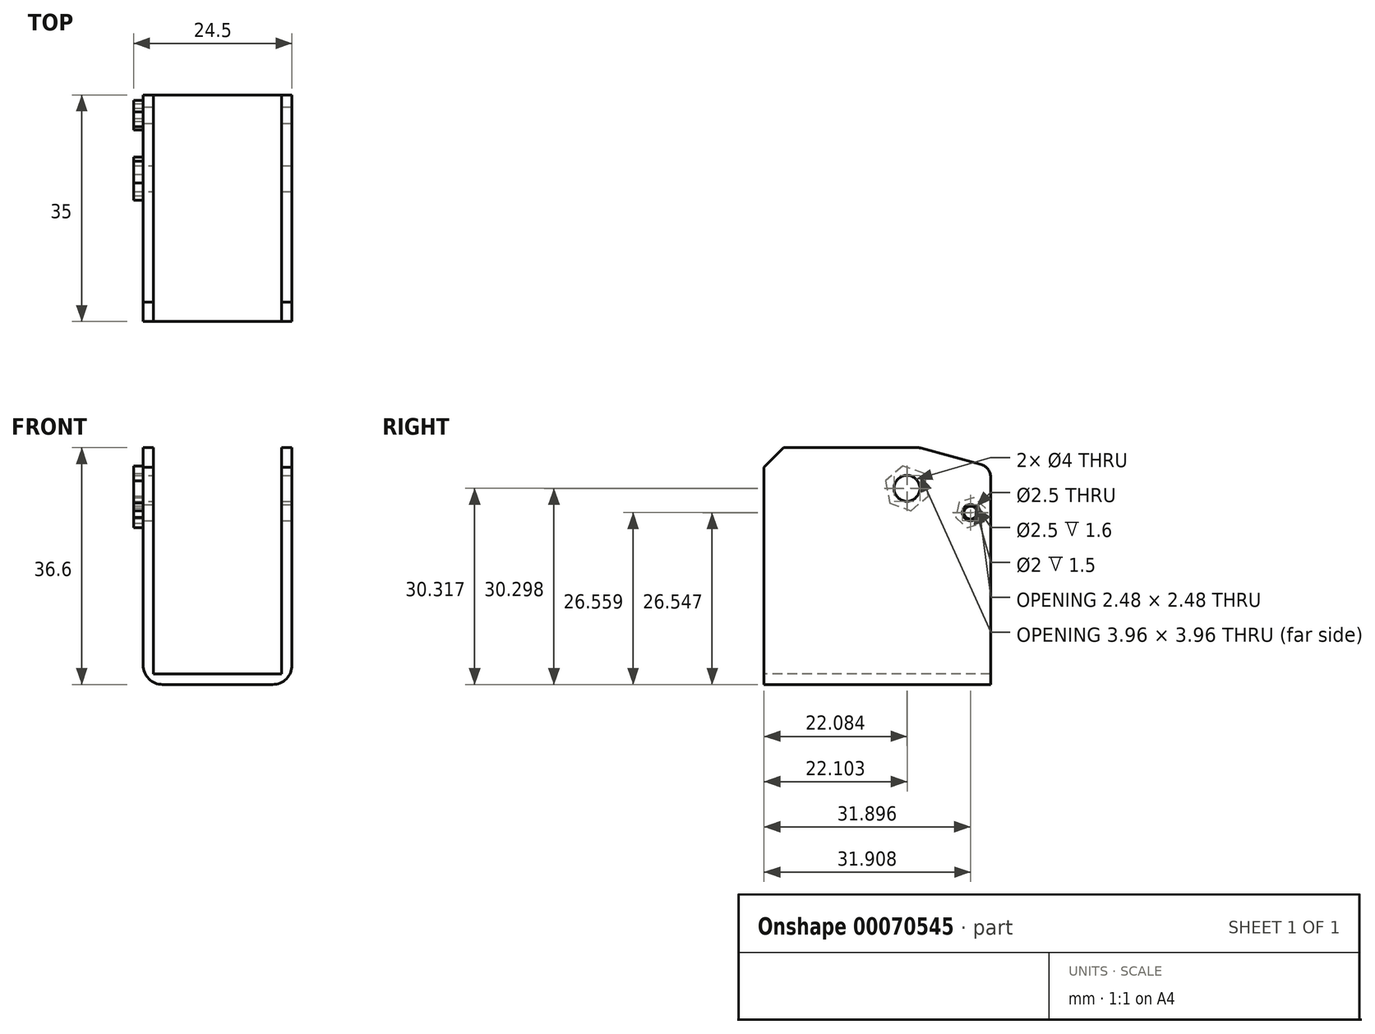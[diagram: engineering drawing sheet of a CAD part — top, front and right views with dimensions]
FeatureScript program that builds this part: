
annotation { "Feature Type Name" : "Feature", "Feature Type Description" : "" }
export const myFeature = defineFeature(function(context is Context, id is Id, definition is map)
    precondition{}
    {
        {
            var Q0;
            Q0=qCreatedBy(makeId("Top.planeOp"),FACE);
            var sketch = newSketch(context, id + "F0", { "sketchPlane" : qUnion([Q0])});
            skLineSegment(sketch, "E0.bottom", {"start": v(-7.08, 17.17) * mm, "end": v(15.92, 17.17) * mm});
            skLineSegment(sketch, "E0.top", {"start": v(-7.08, -17.83) * mm, "end": v(15.92, -17.83) * mm});
            skLineSegment(sketch, "E0.left", {"start": v(-7.08, 17.17) * mm, "end": v(-7.08, -17.83) * mm});
            skLineSegment(sketch, "E0.right", {"start": v(15.92, 17.17) * mm, "end": v(15.92, -17.83) * mm});
            skSolve(sketch);
        }
        {
            var Q0;
            Q0 = qSketchRegion(id + "F0", true);
            extrude(context, id + "F1", {"entities" : qUnion([Q0]), "depth" : 1.6 * mm});
        }
        {
            var Q0;
            Q0=makeQuery(id+"F1.opExtrude","CAP_FACE",FACE,{"disambiguationData":[OSD([sQuery(id+"F0.wireOp",EDGE,"E0.bottom"),sQuery(id+"F0.wireOp",EDGE,"E0.top"),sQuery(id+"F0.wireOp",EDGE,"E0.left"),sQuery(id+"F0.wireOp",EDGE,"E0.right")])],"isStart":false});
            var sketch = newSketch(context, id + "F2", { "sketchPlane" : qUnion([Q0])});
            skLineSegment(sketch, "E1.bottom", {"start": v(-7.08, 17.17) * mm, "end": v(-5.48, 17.17) * mm});
            skLineSegment(sketch, "E1.top", {"start": v(-7.08, -17.83) * mm, "end": v(-5.48, -17.83) * mm});
            skLineSegment(sketch, "E1.left", {"start": v(-7.08, 17.17) * mm, "end": v(-7.08, -17.83) * mm});
            skLineSegment(sketch, "E1.right", {"start": v(-5.48, 17.17) * mm, "end": v(-5.48, -17.83) * mm});
            skLineSegment(sketch, "E2.bottom", {"start": v(15.92, 17.17) * mm, "end": v(14.32, 17.17) * mm});
            skLineSegment(sketch, "E2.top", {"start": v(15.92, -17.83) * mm, "end": v(14.32, -17.83) * mm});
            skLineSegment(sketch, "E2.left", {"start": v(15.92, 17.17) * mm, "end": v(15.92, -17.83) * mm});
            skLineSegment(sketch, "E2.right", {"start": v(14.32, 17.17) * mm, "end": v(14.32, -17.83) * mm});
            skSolve(sketch);
        }
        {
            var Q0;
            Q0 = qSketchRegion(id + "F2", true);
            extrude(context, id + "F3", {"entities" : qUnion([Q0]), "operationType" : NewBodyOperationType.ADD, "depth" : 35 * mm});
        }
        {
            var Q0;
            Q0=makeQuery(id+"F3.opExtrude","CAP_EDGE",EDGE,{"disambiguationData":[OSD([sQuery(id+"F2.wireOp",EDGE,"E2.right")])],"isStart":true});
            var Q1;
            Q1=makeQuery(id+"F1.opExtrude","CAP_EDGE",EDGE,{"disambiguationData":[OSD([sQuery(id+"F0.wireOp",EDGE,"E0.right")])],"isStart":true});
            var Q2;
            Q2=makeQuery(id+"F1.opExtrude","CAP_EDGE",EDGE,{"disambiguationData":[OSD([sQuery(id+"F0.wireOp",EDGE,"E0.left")])],"isStart":true});
            var Q3;
            Q3=makeQuery(id+"F3.opExtrude","CAP_EDGE",EDGE,{"disambiguationData":[OSD([sQuery(id+"F2.wireOp",EDGE,"E1.right")])],"isStart":true});
            fillet(context, id + "F4", {"entities" : qUnion([Q0, Q1, Q2, Q3]), "radius" : 3 * mm, "tangentPropagation" : true, "allowEdgeOverflow" : false});
        }
        {
            var Q0;
            Q0=makeQuery(id+"F3.opExtrude","CAP_EDGE",EDGE,{"disambiguationData":[OSD([sQuery(id+"F2.wireOp",EDGE,"E2.bottom")])],"isStart":false});
            var Q1;
            Q1=makeQuery(id+"F3.opExtrude","CAP_EDGE",EDGE,{"disambiguationData":[OSD([sQuery(id+"F2.wireOp",EDGE,"E1.bottom")])],"isStart":false});
            chamfer(context, id + "F5", {"entities" : qUnion([Q0, Q1]), "chamferType" : ChamferType.TWO_OFFSETS, "width1" : 3 * mm, "oppositeDirection" : false, "width2" : 11 * mm, "tangentPropagation" : true});
        }
        {
            var Q0;
            {var subQ0=sQuery(id+"F2.wireOp",EDGE,"E2.bottom");Q0=makeQuery(id+"F5.opChamfer","BLEND_EDGE",EDGE,{"blendedFrom":[makeQuery(id+"F3.opExtrude","CAP_EDGE",EDGE,{"disambiguationData":[OSD([subQ0])],"isStart":false}),makeQuery(id+"F3.boolean.opBoolean","MERGE",FACE,{"derivedFrom":[makeQuery(id+"F1.opExtrude","SWEPT_FACE",FACE,{"disambiguationData":[OSD([sQuery(id+"F0.wireOp",EDGE,"E0.bottom")])]}),makeQuery(id+"F3.opExtrude","SWEPT_FACE",FACE,{"disambiguationData":[OSD([sQuery(id+"F2.wireOp",EDGE,"E1.bottom")])]}),makeQuery(id+"F3.opExtrude","SWEPT_FACE",FACE,{"disambiguationData":[OSD([subQ0])]})]})],"blendedInto":[makeQuery(id+"F3.boolean.opBoolean","MERGE",FACE,{"derivedFrom":[makeQuery(id+"F1.opExtrude","SWEPT_FACE",FACE,{"disambiguationData":[OSD([sQuery(id+"F0.wireOp",EDGE,"E0.bottom")])]}),makeQuery(id+"F3.opExtrude","SWEPT_FACE",FACE,{"disambiguationData":[OSD([sQuery(id+"F2.wireOp",EDGE,"E1.bottom")])]}),makeQuery(id+"F3.opExtrude","SWEPT_FACE",FACE,{"disambiguationData":[OSD([subQ0])]})]})]});}
            var Q1;
            {var subQ0=sQuery(id+"F2.wireOp",EDGE,"E1.bottom");Q1=makeQuery(id+"F5.opChamfer","BLEND_EDGE",EDGE,{"blendedFrom":[makeQuery(id+"F3.opExtrude","CAP_EDGE",EDGE,{"disambiguationData":[OSD([subQ0])],"isStart":false}),makeQuery(id+"F3.boolean.opBoolean","MERGE",FACE,{"derivedFrom":[makeQuery(id+"F1.opExtrude","SWEPT_FACE",FACE,{"disambiguationData":[OSD([sQuery(id+"F0.wireOp",EDGE,"E0.bottom")])]}),makeQuery(id+"F3.opExtrude","SWEPT_FACE",FACE,{"disambiguationData":[OSD([subQ0])]}),makeQuery(id+"F3.opExtrude","SWEPT_FACE",FACE,{"disambiguationData":[OSD([sQuery(id+"F2.wireOp",EDGE,"E2.bottom")])]})]})],"blendedInto":[makeQuery(id+"F3.boolean.opBoolean","MERGE",FACE,{"derivedFrom":[makeQuery(id+"F1.opExtrude","SWEPT_FACE",FACE,{"disambiguationData":[OSD([sQuery(id+"F0.wireOp",EDGE,"E0.bottom")])]}),makeQuery(id+"F3.opExtrude","SWEPT_FACE",FACE,{"disambiguationData":[OSD([subQ0])]}),makeQuery(id+"F3.opExtrude","SWEPT_FACE",FACE,{"disambiguationData":[OSD([sQuery(id+"F2.wireOp",EDGE,"E2.bottom")])]})]})]});}
            fillet(context, id + "F6", {"entities" : qUnion([Q0, Q1]), "radius" : 2 * mm, "tangentPropagation" : true, "allowEdgeOverflow" : false});
        }
        {
            var Q0;
            {var subQ0=sQuery(id+"F2.wireOp",EDGE,"E2.bottom");Q0=makeQuery(id+"F5.opChamfer","BLEND_EDGE",EDGE,{"blendedFrom":[makeQuery(id+"F3.opExtrude","CAP_EDGE",EDGE,{"disambiguationData":[OSD([subQ0])],"isStart":false}),makeQuery(id+"F3.opExtrude","CAP_FACE",FACE,{"disambiguationData":[OSD([subQ0,sQuery(id+"F2.wireOp",EDGE,"E2.top"),sQuery(id+"F2.wireOp",EDGE,"E2.left"),sQuery(id+"F2.wireOp",EDGE,"E2.right")])],"isStart":false})],"blendedInto":[makeQuery(id+"F3.opExtrude","CAP_FACE",FACE,{"disambiguationData":[OSD([subQ0,sQuery(id+"F2.wireOp",EDGE,"E2.top"),sQuery(id+"F2.wireOp",EDGE,"E2.left"),sQuery(id+"F2.wireOp",EDGE,"E2.right")])],"isStart":false})]});}
            var Q1;
            {var subQ0=sQuery(id+"F2.wireOp",EDGE,"E1.bottom");Q1=makeQuery(id+"F5.opChamfer","BLEND_EDGE",EDGE,{"blendedFrom":[makeQuery(id+"F3.opExtrude","CAP_EDGE",EDGE,{"disambiguationData":[OSD([subQ0])],"isStart":false}),makeQuery(id+"F3.opExtrude","CAP_FACE",FACE,{"disambiguationData":[OSD([subQ0,sQuery(id+"F2.wireOp",EDGE,"E1.top"),sQuery(id+"F2.wireOp",EDGE,"E1.left"),sQuery(id+"F2.wireOp",EDGE,"E1.right")])],"isStart":false})],"blendedInto":[makeQuery(id+"F3.opExtrude","CAP_FACE",FACE,{"disambiguationData":[OSD([subQ0,sQuery(id+"F2.wireOp",EDGE,"E1.top"),sQuery(id+"F2.wireOp",EDGE,"E1.left"),sQuery(id+"F2.wireOp",EDGE,"E1.right")])],"isStart":false})]});}
            fillet(context, id + "F7", {"entities" : qUnion([Q0, Q1]), "radius" : 2 * mm, "tangentPropagation" : true, "allowEdgeOverflow" : false});
        }
        {
            var Q0;
            Q0=makeQuery(id+"F3.opExtrude","CAP_EDGE",EDGE,{"disambiguationData":[OSD([sQuery(id+"F2.wireOp",EDGE,"E1.top")])],"isStart":false});
            var Q1;
            Q1=makeQuery(id+"F3.opExtrude","CAP_EDGE",EDGE,{"disambiguationData":[OSD([sQuery(id+"F2.wireOp",EDGE,"E2.top")])],"isStart":false});
            chamfer(context, id + "F8", {"entities" : qUnion([Q0, Q1]), "width" : 3 * mm, "tangentPropagation" : true});
        }
        {
            var Q0;
            Q0=makeQuery(id+"F3.boolean.opBoolean","MERGE",FACE,{"derivedFrom":[makeQuery(id+"F1.opExtrude","SWEPT_FACE",FACE,{"disambiguationData":[OSD([sQuery(id+"F0.wireOp",EDGE,"E0.right")])]}),makeQuery(id+"F3.opExtrude","SWEPT_FACE",FACE,{"disambiguationData":[OSD([sQuery(id+"F2.wireOp",EDGE,"E2.left")])]})]});
            var sketch = newSketch(context, id + "F9", { "sketchPlane" : qUnion([Q0])});
            skLineSegment(sketch, "E3", {"start": v(4.25, 36.4) * mm, "end": v(4.25, 24.23) * mm, "construction": true});
            skLineSegment(sketch, "E4", {"start": v(14.07, 25.7) * mm, "end": v(14.07, 20.92) * mm, "construction": true});
            skCircle(sketch, "E5", {"center": v(4.25, 30.32) * mm, "radius": 2 * mm});
            skCircle(sketch, "E6", {"center": v(14.07, 26.56) * mm, "radius": 1.25 * mm});
            skSolve(sketch);
        }
        {
            var Q0;
            Q0 = qSketchRegion(id + "F9", true);
            extrude(context, id + "F10", {"entities" : qUnion([Q0]), "operationType" : NewBodyOperationType.REMOVE, "oppositeDirection" : true, "depth" : 30 * mm});
        }
        {
            var Q0;
            Q0=makeQuery(id+"F3.boolean.opBoolean","MERGE",FACE,{"derivedFrom":[makeQuery(id+"F1.opExtrude","SWEPT_FACE",FACE,{"disambiguationData":[OSD([sQuery(id+"F0.wireOp",EDGE,"E0.left")])]}),makeQuery(id+"F3.opExtrude","SWEPT_FACE",FACE,{"disambiguationData":[OSD([sQuery(id+"F2.wireOp",EDGE,"E1.left")])]})]});
            var sketch = newSketch(context, id + "F11", { "sketchPlane" : qUnion([Q0])});
            skCircle(sketch, "E7.cCircle", {"center": v(-4.25, 30.32) * mm, "radius": 3.04 * mm, "construction": true});
            skLineSegment(sketch, "E7.0", {"start": v(-7.57, 29.15) * mm, "end": v(-6.92, 32.6) * mm});
            skLineSegment(sketch, "E7.1", {"start": v(-6.92, 32.6) * mm, "end": v(-3.61, 33.77) * mm});
            skLineSegment(sketch, "E7.2", {"start": v(-3.61, 33.77) * mm, "end": v(-0.94, 31.49) * mm});
            skLineSegment(sketch, "E7.3", {"start": v(-0.94, 31.49) * mm, "end": v(-1.58, 28.03) * mm});
            skLineSegment(sketch, "E7.4", {"start": v(-1.58, 28.03) * mm, "end": v(-4.9, 26.86) * mm});
            skLineSegment(sketch, "E7.5", {"start": v(-4.9, 26.86) * mm, "end": v(-7.57, 29.15) * mm});
            skPoint(sketch, "E7.0.midPoint", {"position": v(-7.25, 30.87) * mm});
            skCircle(sketch, "E8.cCircle", {"center": v(-14.07, 26.56) * mm, "radius": 2.07 * mm, "construction": true});
            skLineSegment(sketch, "E8.0", {"start": v(-16.34, 27.29) * mm, "end": v(-14.57, 28.9) * mm});
            skLineSegment(sketch, "E8.1", {"start": v(-14.57, 28.9) * mm, "end": v(-12.3, 28.17) * mm});
            skLineSegment(sketch, "E8.2", {"start": v(-12.3, 28.17) * mm, "end": v(-11.8, 25.83) * mm});
            skLineSegment(sketch, "E8.3", {"start": v(-11.8, 25.83) * mm, "end": v(-13.56, 24.22) * mm});
            skLineSegment(sketch, "E8.4", {"start": v(-13.56, 24.22) * mm, "end": v(-15.83, 24.95) * mm});
            skLineSegment(sketch, "E8.5", {"start": v(-15.83, 24.95) * mm, "end": v(-16.34, 27.29) * mm});
            skPoint(sketch, "E8.0.midPoint", {"position": v(-15.46, 28.1) * mm});
            skSolve(sketch);
        }
        {
            var Q0;
            Q0 = qSketchRegion(id + "F11", true);
            extrude(context, id + "F12", {"entities" : qUnion([Q0]), "operationType" : NewBodyOperationType.ADD, "depth" : 1.5 * mm});
        }
        {
            var Q0;
            Q0=makeQuery(id+"F3.boolean.opBoolean","MERGE",FACE,{"derivedFrom":[makeQuery(id+"F1.opExtrude","SWEPT_FACE",FACE,{"disambiguationData":[OSD([sQuery(id+"F0.wireOp",EDGE,"E0.left")])]}),makeQuery(id+"F3.opExtrude","SWEPT_FACE",FACE,{"disambiguationData":[OSD([sQuery(id+"F2.wireOp",EDGE,"E1.left")])]})]});
            var sketch = newSketch(context, id + "F13", { "sketchPlane" : qUnion([Q0])});
            skLineSegment(sketch, "E9", {"start": v(-3.24, 27.45) * mm, "end": v(-5.27, 33.19) * mm, "construction": true});
            skLineSegment(sketch, "E10", {"start": v(-2.28, 32.63) * mm, "end": v(-6.23, 28) * mm, "construction": true});
            skLineSegment(sketch, "E11", {"start": v(-6.23, 28) * mm, "end": v(-5.85, 28.02) * mm, "construction": true});
            skLineSegment(sketch, "E12", {"start": v(-5.85, 28.02) * mm, "end": v(-6.23, 28) * mm, "construction": true});
            skLineSegment(sketch, "E13", {"start": v(-12.04, 27) * mm, "end": v(-16.09, 26.12) * mm, "construction": true});
            skLineSegment(sketch, "E14", {"start": v(-15.46, 28.1) * mm, "end": v(-12.67, 25.03) * mm, "construction": true});
            skCircle(sketch, "E15", {"center": v(-4.25, 30.32) * mm, "radius": 2 * mm});
            skCircle(sketch, "E16", {"center": v(-14.07, 26.56) * mm, "radius": 1 * mm});
            skSolve(sketch);
        }
        {
            var Q0;
            Q0 = qSketchRegion(id + "F13", true);
            extrude(context, id + "F14", {"entities" : qUnion([Q0]), "operationType" : NewBodyOperationType.REMOVE, "oppositeDirection" : true, "depth" : 25 * mm, "hasSecondDirection" : true, "secondDirectionOppositeDirection" : false, "secondDirectionDepth" : 25 * mm});
        }
    });
